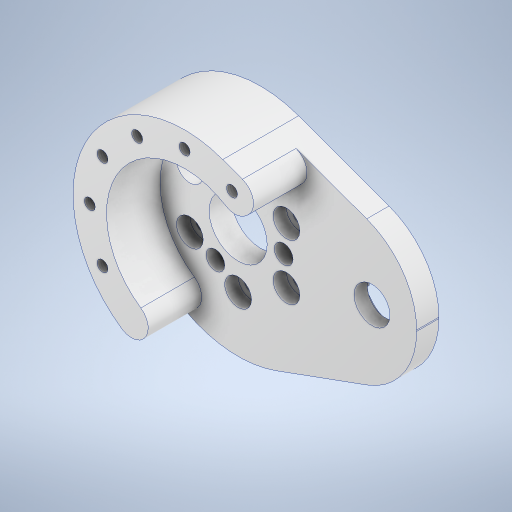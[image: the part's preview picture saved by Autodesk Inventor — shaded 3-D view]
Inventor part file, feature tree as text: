
AUTODESK INVENTOR PART (.ipt)
format: ipt  version: 2024.3 (Build 283343000, 343)  size: 516,608 bytes
history: native  units: mm
features: sketch x8, extrude x4, hole x4, other x2, fillet x2
ambient origin geometry x8: Origin, YZ Plane, XZ Plane, XY Plane, X Axis, Y Axis, Z Axis, Center Point
bodies: Body1 (feature_tree)
feature tree (20):
  other  "ソリッド1"
  other  "作業平面1"
  extrude  "押し出し9"  Depth=50.0mm
  extrude  "押し出し10"  Depth=8.05mm
  extrude  "押し出し11"  Depth=30.0mm
  hole  "穴5"  [1 undecoded]
  hole  "穴6"  [1 undecoded]
  extrude  "押し出し12"  Depth=25.0mm
  hole  "穴7"  [1 undecoded]
  fillet  "フィレット9"  Radius=5.0mm
  hole  "穴8"  [1 undecoded]
  fillet  "フィレット12"  Radius=2.0mm
  sketch  "スケッチ14"
  sketch  "スケッチ15"
  sketch  "スケッチ16"
  sketch  "スケッチ17"
  sketch  "スケッチ18"
  sketch  "スケッチ19"
  sketch  "スケッチ20"
  sketch  "スケッチ21"
note: 4 required parameter values undecoded (feature->parameter linkage not recoverable at this tier; creation-order binding heuristic only, values carry confidence <= 0.55)
